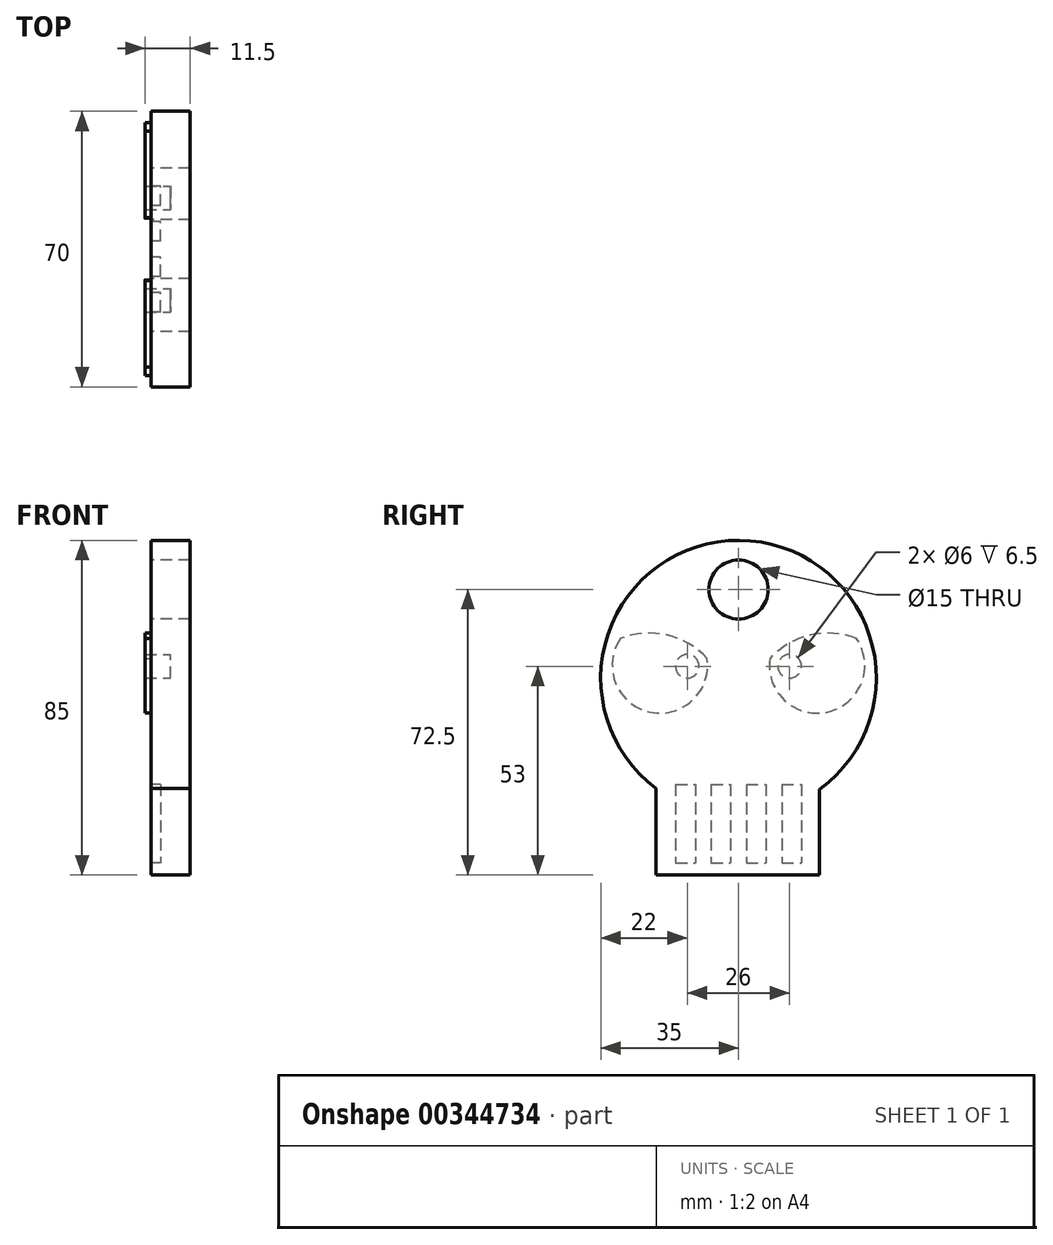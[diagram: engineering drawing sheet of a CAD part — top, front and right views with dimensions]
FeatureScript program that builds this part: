
annotation { "Feature Type Name" : "Feature", "Feature Type Description" : "" }
export const myFeature = defineFeature(function(context is Context, id is Id, definition is map)
    precondition{}
    {
        {
            var Q0;
            Q0=qCreatedBy(makeId("Right.planeOp"),FACE);
            var sketch = newSketch(context, id + "F0", { "sketchPlane" : qUnion([Q0])});
            skCircle(sketch, "E0", {"center": v(0, 15) * mm, "radius": 35 * mm});
            skLineSegment(sketch, "E1.bottom", {"start": v(-20.94, -5) * mm, "end": v(20.61, -5) * mm});
            skLineSegment(sketch, "E1.top", {"start": v(-20.94, -35) * mm, "end": v(20.61, -35) * mm});
            skLineSegment(sketch, "E1.left", {"start": v(-20.94, -5) * mm, "end": v(-20.94, -35) * mm});
            skLineSegment(sketch, "E1.right", {"start": v(20.61, -5) * mm, "end": v(20.61, -35) * mm});
            skArc(sketch, "E2", {"start": v(-8, 20) * mm, "mid": v(-18.23, 25.9) * mm, "end": v(-30, 25) * mm});
            skArc(sketch, "E3", {"start": v(30, 25) * mm, "mid": v(18.23, 25.9) * mm, "end": v(8, 20) * mm});
            skArc(sketch, "E4", {"start": v(8, 20) * mm, "mid": v(22.66, 6.4) * mm, "end": v(30, 25) * mm});
            skArc(sketch, "E5", {"start": v(-30, 25) * mm, "mid": v(-22.66, 6.4) * mm, "end": v(-8, 20) * mm});
            skCircle(sketch, "E6", {"center": v(-13, 18) * mm, "radius": 3 * mm});
            skCircle(sketch, "E7", {"center": v(13, 18) * mm, "radius": 3 * mm});
            skSolve(sketch);
        }
        {
            var Q0;
            {var subQ5=sQuery(id+"F0.wireOp",EDGE,"E1.bottom");Q0=makeQuery(id+"F0.imprint","IMPRINT",FACE,{"disambiguationData":[TD([[makeQuery(id+"F0.imprint","IMPRINT",EDGE,{"derivedFrom":subQ5}),-1.0]])]});}
            var Q1;
            {var subQ1=sQuery(id+"F0.wireOp",EDGE,"E1.bottom");Q1=makeQuery(id+"F0.imprint","IMPRINT",FACE,{"disambiguationData":[TD([[makeQuery(id+"F0.imprint","IMPRINT",EDGE,{"derivedFrom":subQ1}),1.0]])]});}
            var Q2;
            Q2=makeQuery(id+"F0.imprint","IMPRINT",FACE,{"disambiguationData":[TD([[makeQuery(id+"F0.imprint","IMPRINT",EDGE,{"derivedFrom":sQuery(id+"F0.wireOp",EDGE,"E6")}),1.0]])]});
            var Q3;
            Q3=makeQuery(id+"F0.imprint","IMPRINT",FACE,{"disambiguationData":[TD([[makeQuery(id+"F0.imprint","IMPRINT",EDGE,{"derivedFrom":sQuery(id+"F0.wireOp",EDGE,"E7")}),1.0]])]});
            var Q4;
            {var subQ5=sQuery(id+"F0.wireOp",EDGE,"E1.top");Q4=makeQuery(id+"F0.imprint","IMPRINT",FACE,{"disambiguationData":[TD([[makeQuery(id+"F0.imprint","IMPRINT",EDGE,{"derivedFrom":subQ5}),1.0]])]});}
            var Q5;
            Q5=makeQuery(id+"F0.imprint","IMPRINT",FACE,{"disambiguationData":[TD([[makeQuery(id+"F0.imprint","IMPRINT",EDGE,{"derivedFrom":sQuery(id+"F0.wireOp",EDGE,"E2")}),1.0]])]});
            var Q6;
            Q6=makeQuery(id+"F0.imprint","IMPRINT",FACE,{"disambiguationData":[TD([[makeQuery(id+"F0.imprint","IMPRINT",EDGE,{"derivedFrom":sQuery(id+"F0.wireOp",EDGE,"E3")}),1.0]])]});
            extrude(context, id + "F1", {"entities" : qUnion([Q0, Q1, Q2, Q3, Q4, Q5, Q6]), "depth" : 10 * mm});
        }
        {
            var Q0;
            Q0=makeQuery(id+"F0.imprint","IMPRINT",FACE,{"disambiguationData":[TD([[makeQuery(id+"F0.imprint","IMPRINT",EDGE,{"derivedFrom":sQuery(id+"F0.wireOp",EDGE,"E2")}),1.0]])]});
            var Q1;
            Q1=makeQuery(id+"F0.imprint","IMPRINT",FACE,{"disambiguationData":[TD([[makeQuery(id+"F0.imprint","IMPRINT",EDGE,{"derivedFrom":sQuery(id+"F0.wireOp",EDGE,"E3")}),1.0]])]});
            extrude(context, id + "F2", {"entities" : qUnion([Q0, Q1]), "operationType" : NewBodyOperationType.ADD, "oppositeDirection" : true, "depth" : 1.5 * mm});
        }
        {
            var Q0;
            Q0=makeQuery(id+"F0.imprint","IMPRINT",FACE,{"disambiguationData":[TD([[makeQuery(id+"F0.imprint","IMPRINT",EDGE,{"derivedFrom":sQuery(id+"F0.wireOp",EDGE,"E6")}),1.0]])]});
            var Q1;
            Q1=makeQuery(id+"F0.imprint","IMPRINT",FACE,{"disambiguationData":[TD([[makeQuery(id+"F0.imprint","IMPRINT",EDGE,{"derivedFrom":sQuery(id+"F0.wireOp",EDGE,"E7")}),1.0]])]});
            extrude(context, id + "F3", {"entities" : qUnion([Q0, Q1]), "operationType" : NewBodyOperationType.REMOVE, "depth" : 5 * mm});
        }
        {
            var Q0;
            {var subQ5=sQuery(id+"F0.wireOp",EDGE,"E1.top");Q0=makeQuery(id+"F0.imprint","IMPRINT",FACE,{"disambiguationData":[TD([[makeQuery(id+"F0.imprint","IMPRINT",EDGE,{"derivedFrom":subQ5}),1.0]])]});}
            var sketch = newSketch(context, id + "F4", { "sketchPlane" : qUnion([Q0])});
            skLineSegment(sketch, "E8.bottom", {"start": v(-16, -12) * mm, "end": v(-11, -12) * mm});
            skLineSegment(sketch, "E8.top", {"start": v(-16, -32) * mm, "end": v(-11, -32) * mm});
            skLineSegment(sketch, "E8.left", {"start": v(-16, -12) * mm, "end": v(-16, -32) * mm});
            skLineSegment(sketch, "E8.right", {"start": v(-11, -12) * mm, "end": v(-11, -32) * mm});
            skLineSegment(sketch, "E9.bottom", {"start": v(-7, -12) * mm, "end": v(-2, -12) * mm});
            skLineSegment(sketch, "E9.top", {"start": v(-7, -32) * mm, "end": v(-2, -32) * mm});
            skLineSegment(sketch, "E9.left", {"start": v(-7, -12) * mm, "end": v(-7, -32) * mm});
            skLineSegment(sketch, "E9.right", {"start": v(-2, -12) * mm, "end": v(-2, -32) * mm});
            skLineSegment(sketch, "E10.bottom", {"start": v(2, -12) * mm, "end": v(7, -12) * mm});
            skLineSegment(sketch, "E10.top", {"start": v(2, -32) * mm, "end": v(7, -32) * mm});
            skLineSegment(sketch, "E10.left", {"start": v(2, -12) * mm, "end": v(2, -32) * mm});
            skLineSegment(sketch, "E10.right", {"start": v(7, -12) * mm, "end": v(7, -32) * mm});
            skLineSegment(sketch, "E11.bottom", {"start": v(11, -12) * mm, "end": v(16, -12) * mm});
            skLineSegment(sketch, "E11.top", {"start": v(11, -32) * mm, "end": v(16, -32) * mm});
            skLineSegment(sketch, "E11.left", {"start": v(11, -12) * mm, "end": v(11, -32) * mm});
            skLineSegment(sketch, "E11.right", {"start": v(16, -12) * mm, "end": v(16, -32) * mm});
            skSolve(sketch);
        }
        {
            var Q0;
            {var subQ0=sQuery(id+"F4.wireOp",EDGE,"E8.bottom");Q0=makeQuery(id+"F4.imprint","IMPRINT",FACE,{"disambiguationData":[TD([[makeQuery(id+"F4.imprint","IMPRINT",EDGE,{"derivedFrom":subQ0}),-1.0]])]});}
            var Q1;
            {var subQ0=sQuery(id+"F4.wireOp",EDGE,"E9.bottom");Q1=makeQuery(id+"F4.imprint","IMPRINT",FACE,{"disambiguationData":[TD([[makeQuery(id+"F4.imprint","IMPRINT",EDGE,{"derivedFrom":subQ0}),-1.0]])]});}
            var Q2;
            {var subQ0=sQuery(id+"F4.wireOp",EDGE,"E10.bottom");Q2=makeQuery(id+"F4.imprint","IMPRINT",FACE,{"disambiguationData":[TD([[makeQuery(id+"F4.imprint","IMPRINT",EDGE,{"derivedFrom":subQ0}),-1.0]])]});}
            var Q3;
            {var subQ0=sQuery(id+"F4.wireOp",EDGE,"E11.bottom");Q3=makeQuery(id+"F4.imprint","IMPRINT",FACE,{"disambiguationData":[TD([[makeQuery(id+"F4.imprint","IMPRINT",EDGE,{"derivedFrom":subQ0}),-1.0]])]});}
            var Q4;
            {var subQ0=sQuery(id+"F4.wireOp",EDGE,"E11.top");Q4=makeQuery(id+"F4.imprint","IMPRINT",FACE,{"disambiguationData":[TD([[makeQuery(id+"F4.imprint","IMPRINT",EDGE,{"derivedFrom":subQ0}),1.0]])]});}
            var Q5;
            {var subQ0=sQuery(id+"F4.wireOp",EDGE,"E8.top");Q5=makeQuery(id+"F4.imprint","IMPRINT",FACE,{"disambiguationData":[TD([[makeQuery(id+"F4.imprint","IMPRINT",EDGE,{"derivedFrom":subQ0}),1.0]])]});}
            var Q6;
            {var subQ0=sQuery(id+"F4.wireOp",EDGE,"E10.top");Q6=makeQuery(id+"F4.imprint","IMPRINT",FACE,{"disambiguationData":[TD([[makeQuery(id+"F4.imprint","IMPRINT",EDGE,{"derivedFrom":subQ0}),1.0]])]});}
            var Q7;
            {var subQ0=sQuery(id+"F4.wireOp",EDGE,"E9.top");Q7=makeQuery(id+"F4.imprint","IMPRINT",FACE,{"disambiguationData":[TD([[makeQuery(id+"F4.imprint","IMPRINT",EDGE,{"derivedFrom":subQ0}),1.0]])]});}
            extrude(context, id + "F5", {"entities" : qUnion([Q0, Q1, Q2, Q3, Q4, Q5, Q6, Q7]), "operationType" : NewBodyOperationType.REMOVE, "depth" : 2.5 * mm});
        }
        {
            var Q0;
            {var subQ1=sQuery(id+"F0.wireOp",EDGE,"E1.bottom");Q0=makeQuery(id+"F0.imprint","IMPRINT",FACE,{"disambiguationData":[TD([[makeQuery(id+"F0.imprint","IMPRINT",EDGE,{"derivedFrom":subQ1}),1.0]])]});}
            var sketch = newSketch(context, id + "F6", { "sketchPlane" : qUnion([Q0])});
            skCircle(sketch, "E12", {"center": v(0, 37.5) * mm, "radius": 7.5 * mm});
            skSolve(sketch);
        }
        {
            var Q0;
            Q0 = qSketchRegion(id + "F6", true);
            extrude(context, id + "F7", {"entities" : qUnion([Q0]), "operationType" : NewBodyOperationType.REMOVE, "depth" : 39.2 * mm});
        }
    });
